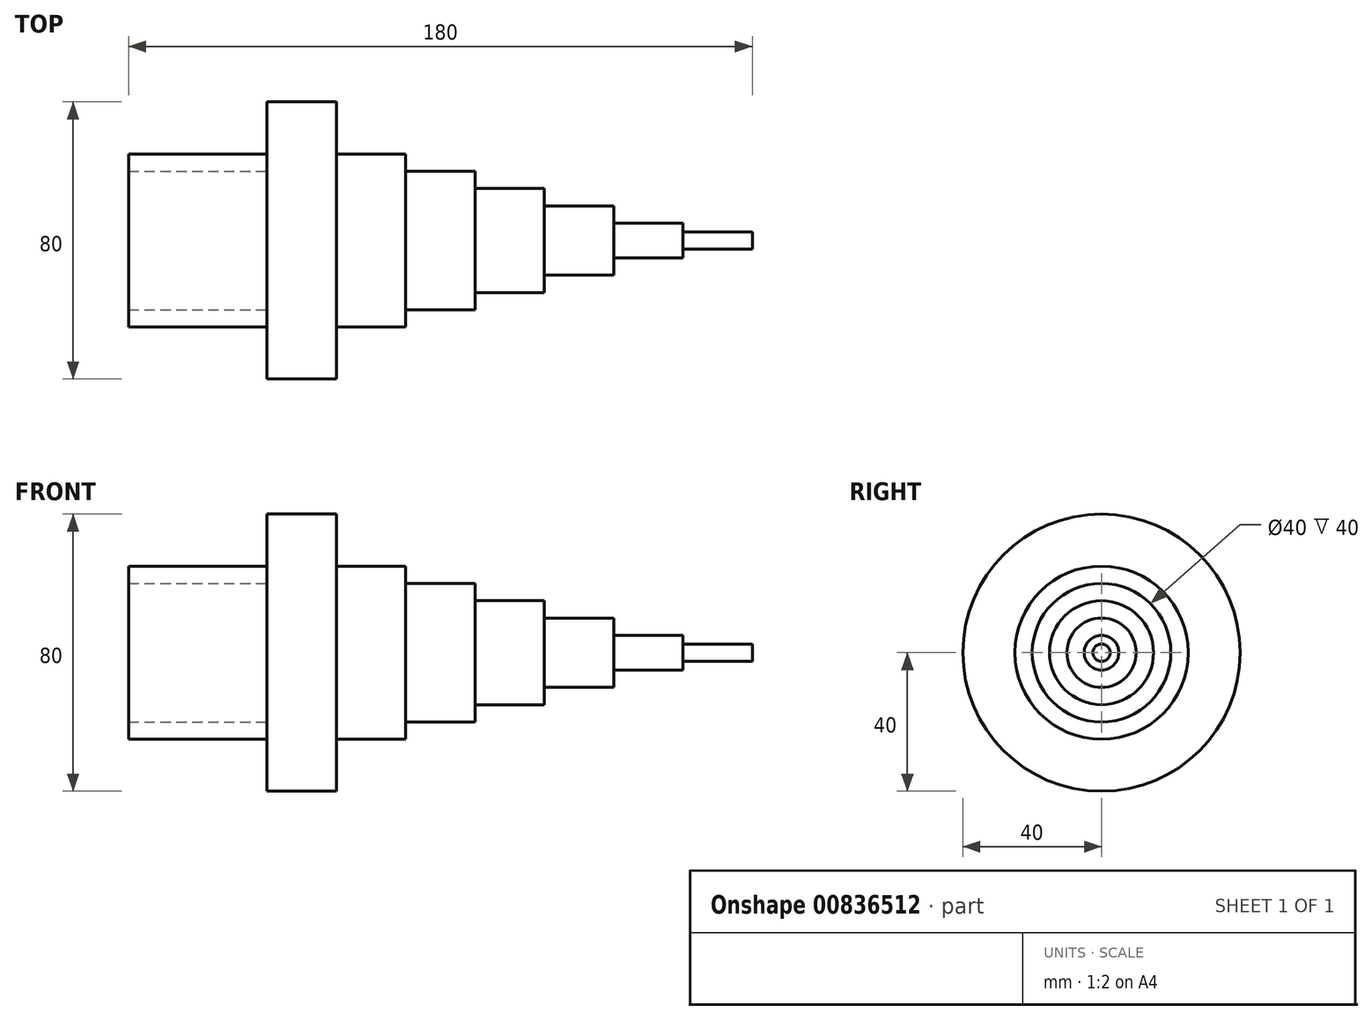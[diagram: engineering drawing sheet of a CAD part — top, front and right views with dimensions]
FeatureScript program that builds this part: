
annotation { "Feature Type Name" : "Feature", "Feature Type Description" : "" }
export const myFeature = defineFeature(function(context is Context, id is Id, definition is map)
    precondition{}
    {
        {
            var Q0;
            Q0=qCreatedBy(makeId("Top.planeOp"),FACE);
            var sketch = newSketch(context, id + "F0", { "sketchPlane" : qUnion([Q0])});
            skLineSegment(sketch, "E0", {"start": v(-80, 20) * mm, "end": v(-80, 25) * mm});
            skLineSegment(sketch, "E1", {"start": v(-80, 25) * mm, "end": v(-40, 25) * mm});
            skLineSegment(sketch, "E2", {"start": v(-40, 25) * mm, "end": v(-40, 40) * mm});
            skLineSegment(sketch, "E3", {"start": v(-40, 40) * mm, "end": v(-20, 40) * mm});
            skLineSegment(sketch, "E4", {"start": v(-20, 40) * mm, "end": v(-20, 25) * mm});
            skLineSegment(sketch, "E5", {"start": v(-20, 25) * mm, "end": v(0, 25) * mm});
            skLineSegment(sketch, "E6", {"start": v(0, 25) * mm, "end": v(0, 20) * mm});
            skLineSegment(sketch, "E7", {"start": v(0, 20) * mm, "end": v(20, 20) * mm});
            skLineSegment(sketch, "E8", {"start": v(20, 20) * mm, "end": v(20, 15) * mm});
            skLineSegment(sketch, "E9", {"start": v(20, 15) * mm, "end": v(40, 15) * mm});
            skLineSegment(sketch, "E10", {"start": v(40, 15) * mm, "end": v(40, 10) * mm});
            skLineSegment(sketch, "E11", {"start": v(40, 10) * mm, "end": v(60, 10) * mm});
            skLineSegment(sketch, "E12", {"start": v(60, 10) * mm, "end": v(60, 5) * mm});
            skLineSegment(sketch, "E13", {"start": v(60, 5) * mm, "end": v(80, 5) * mm});
            skLineSegment(sketch, "E14", {"start": v(80, 5) * mm, "end": v(80, 2.5) * mm});
            skLineSegment(sketch, "E15", {"start": v(80, 2.5) * mm, "end": v(100, 2.5) * mm});
            skLineSegment(sketch, "E16", {"start": v(100, 2.5) * mm, "end": v(100, 0) * mm});
            skLineSegment(sketch, "E17", {"start": v(100, 0) * mm, "end": v(-40, 0) * mm});
            skLineSegment(sketch, "E18", {"start": v(-40, 0) * mm, "end": v(-40, 20) * mm});
            skLineSegment(sketch, "E19", {"start": v(-80, 20) * mm, "end": v(-40, 20) * mm});
            skSolve(sketch);
        }
        {
            var Q0;
            Q0=makeQuery(id+"F0.imprint","IMPRINT",FACE,{"disambiguationData":[TD([[makeQuery(id+"F0.imprint","IMPRINT",EDGE,{"derivedFrom":sQuery(id+"F0.wireOp",EDGE,"E0")}),-1.0]])]});
            var Q1;
            Q1=sQuery(id+"F0.wireOp",EDGE,"E17");
            revolve(context, id + "F1", {"surfaceOperationType" : NewSurfaceOperationType.NEW, "entities" : qUnion([Q0]), "axis" : qUnion([Q1]), "revolveType" : RevolveType.FULL});
        }
    });
